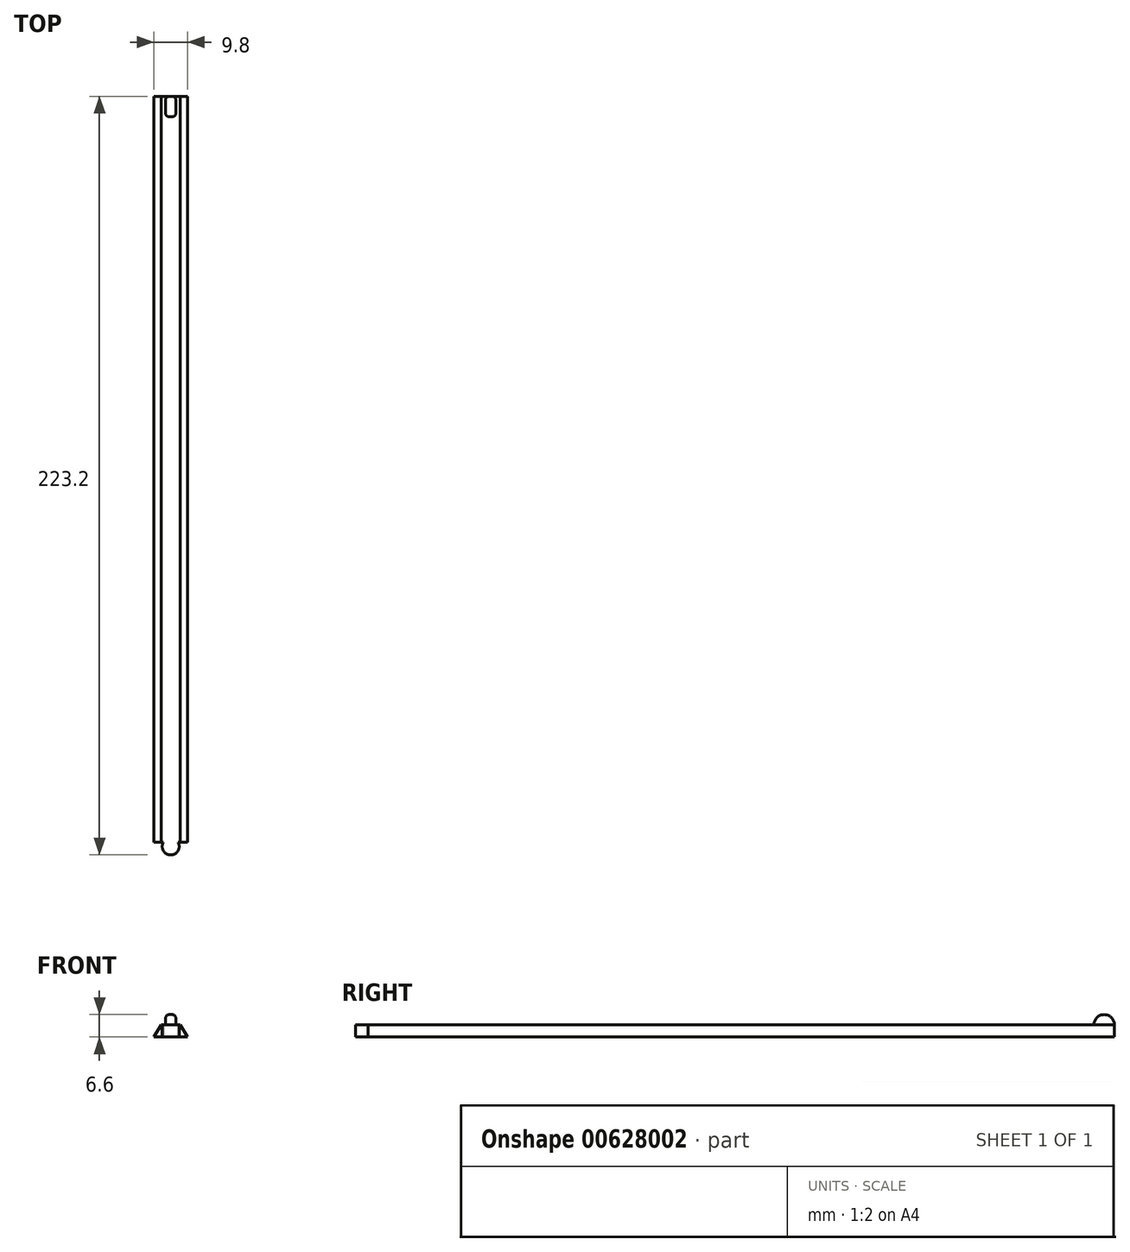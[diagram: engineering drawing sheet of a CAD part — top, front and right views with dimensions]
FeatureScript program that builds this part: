
annotation { "Feature Type Name" : "Feature", "Feature Type Description" : "" }
export const myFeature = defineFeature(function(context is Context, id is Id, definition is map)
    precondition{}
    {
        {
            var Q0;
            Q0=qCreatedBy(makeId("Front.planeOp"),FACE);
            var sketch = newSketch(context, id + "F0", { "sketchPlane" : qUnion([Q0])});
            skLineSegment(sketch, "E0", {"start": v(0, 0) * mm, "end": v(9.8, 0) * mm});
            skLineSegment(sketch, "E1", {"start": v(9.8, 0) * mm, "end": v(7.72, 3.6) * mm});
            skLineSegment(sketch, "E2", {"start": v(7.72, 3.6) * mm, "end": v(2.08, 3.6) * mm});
            skLineSegment(sketch, "E3", {"start": v(2.08, 3.6) * mm, "end": v(0, 0) * mm});
            skSolve(sketch);
        }
        {
            var Q0;
            Q0=makeQuery(id+"F0.imprint","IMPRINT",FACE,{"disambiguationData":[TD([[makeQuery(id+"F0.imprint","IMPRINT",EDGE,{"derivedFrom":sQuery(id+"F0.wireOp",EDGE,"E0")}),1.0]])]});
            extrude(context, id + "F1", {"entities" : qUnion([Q0]), "depth" : 219.5 * mm, "offsetDistance" : 25 * mm});
        }
        {
            var Q0;
            Q0=makeQuery(id+"F1.opExtrude","SWEPT_FACE",FACE,{"disambiguationData":[OSD([sQuery(id+"F0.wireOp",EDGE,"E0")])]});
            var sketch = newSketch(context, id + "F2", { "sketchPlane" : qUnion([Q0])});
            skCircle(sketch, "E4", {"center": v(4.9, 220.7) * mm, "radius": 2.5 * mm});
            skPoint(sketch, "E4.centerSnap0", {"position": v(4.9, 219.5) * mm});
            skSolve(sketch);
        }
        {
            var Q0;
            {var subQ0=sQuery(id+"F2.wireOp",EDGE,"E4");var subQ1=makeQuery(id+"F1.opExtrude","CAP_EDGE",EDGE,{"disambiguationData":[OSD([sQuery(id+"F0.wireOp",EDGE,"E0")])],"isStart":false});var subQ2=makeQuery(id+"F2.imprint","INTERSECT",VERTEX,{"disambiguationData":[OD(0.0)],"derivedFrom":[subQ1,subQ0]});Q0=makeQuery(id+"F2.imprint","IMPRINT",FACE,{"disambiguationData":[TD([[makeQuery(id+"F2.imprint","IMPRINT",EDGE,{"disambiguationData":[TD([[subQ2,1.0]])],"derivedFrom":subQ0}),1.0]])]});}
            extrude(context, id + "F3", {"entities" : qUnion([Q0]), "operationType" : NewBodyOperationType.ADD, "oppositeDirection" : true, "depth" : 3.6 * mm, "offsetDistance" : 25 * mm});
        }
        {
            var Q0;
            Q0=makeQuery(id+"F1.opExtrude","SWEPT_BODY",BODY,{"disambiguationData":[OSD([sQuery(id+"F0.wireOp",EDGE,"E0"),sQuery(id+"F0.wireOp",EDGE,"E1"),sQuery(id+"F0.wireOp",EDGE,"E2"),sQuery(id+"F0.wireOp",EDGE,"E3")])]});
            transform(context, id + "F4", {"entities" : qUnion([Q0]), "transformType" : TransformType.TRANSLATION_3D, "dx" : 0 * mm, "dy" : 0 * mm, "dz" : 0 * mm, "makeCopy" : true});
        }
        {
            var Q0;
            Q0=makeQuery(id+"F1.opExtrude","SWEPT_BODY",BODY,{"disambiguationData":[OSD([sQuery(id+"F0.wireOp",EDGE,"E0"),sQuery(id+"F0.wireOp",EDGE,"E1"),sQuery(id+"F0.wireOp",EDGE,"E2"),sQuery(id+"F0.wireOp",EDGE,"E3")])]});
            deleteBodies(context, id + "F5", {"entities" : qUnion([Q0])});
        }
        {
            var Q0;
            Q0=makeQuery(id+"F4.opPattern","COPY",FACE,{"derivedFrom":makeQuery(id+"F3.boolean.opBoolean","MERGE",FACE,{"derivedFrom":[makeQuery(id+"F1.opExtrude","SWEPT_FACE",FACE,{"disambiguationData":[OSD([sQuery(id+"F0.wireOp",EDGE,"E2")])]}),makeQuery(id+"F3.opExtrude","CAP_FACE",FACE,{"disambiguationData":[OSD([sQuery(id+"F0.wireOp",EDGE,"E0"),sQuery(id+"F2.wireOp",EDGE,"E4")])],"isStart":false})]}),"instanceName":"1"});
            var sketch = newSketch(context, id + "F6", { "sketchPlane" : qUnion([Q0])});
            skLineSegment(sketch, "E5.bottom", {"start": v(3.4, 0) * mm, "end": v(6.4, 0) * mm});
            skLineSegment(sketch, "E5.top", {"start": v(3.4, -3) * mm, "end": v(6.4, -3) * mm});
            skLineSegment(sketch, "E5.left", {"start": v(3.4, 0) * mm, "end": v(3.4, -3) * mm});
            skLineSegment(sketch, "E5.right", {"start": v(6.4, 0) * mm, "end": v(6.4, -3) * mm});
            skLineSegment(sketch, "E6.0", {"start": v(7.72, 0) * mm, "end": v(2.08, 0) * mm});
            skSolve(sketch);
        }
        {
            var Q0;
            Q0 = qSketchRegion(id + "F6", true);
            var Q1;
            Q1=sQuery(id+"F6.wireOp",EDGE,"E5.top");
            revolve(context, id + "F7", {"operationType" : NewBodyOperationType.ADD, "surfaceOperationType" : NewSurfaceOperationType.NEW, "entities" : qUnion([Q0]), "axis" : qUnion([Q1]), "revolveType" : RevolveType.ONE_DIRECTION, "angle" : 180 * degree});
        }
        {
            var Q0;
            Q0=makeQuery(id+"F7.opRevolve","SWEPT_EDGE",EDGE,{"disambiguationData":[OSD([sQuery(id+"F6.wireOp",EDGE,"E5.right"),sQuery(id+"F6.wireOp",EDGE,"E6.0")])]});
            var Q1;
            Q1=makeQuery(id+"F7.opRevolve","SWEPT_EDGE",EDGE,{"disambiguationData":[OSD([sQuery(id+"F6.wireOp",EDGE,"E5.left"),sQuery(id+"F6.wireOp",EDGE,"E6.0")])]});
            fillet(context, id + "F8", {"entities" : qUnion([Q0, Q1]), "radius" : 1 * mm, "tangentPropagation" : true, "allowEdgeOverflow" : false});
        }
    });
